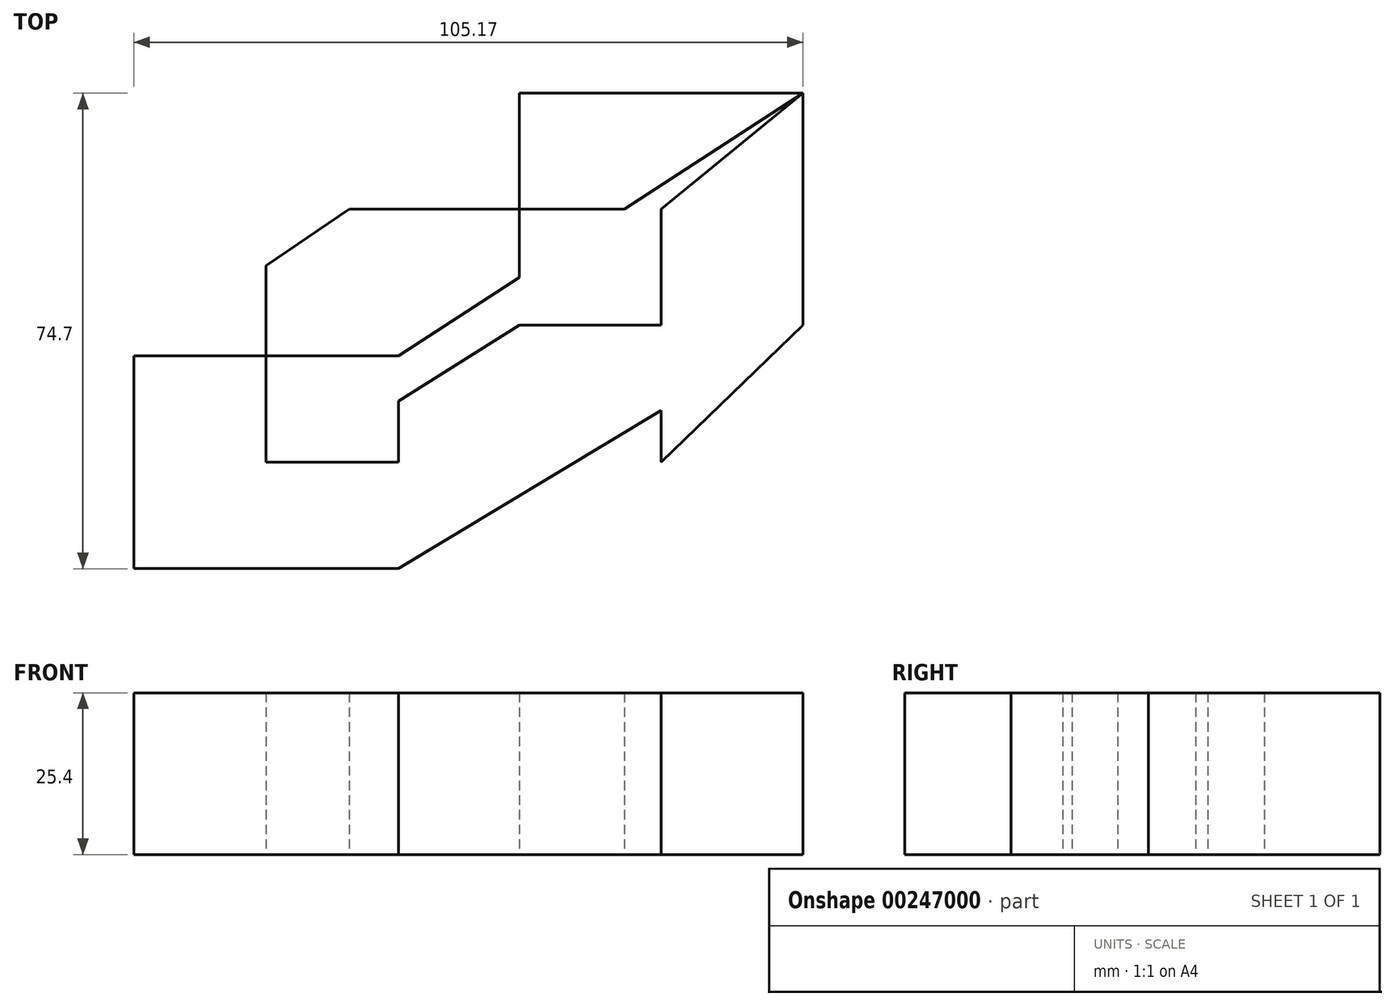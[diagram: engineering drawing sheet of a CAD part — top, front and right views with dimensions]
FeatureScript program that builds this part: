
annotation { "Feature Type Name" : "Feature", "Feature Type Description" : "" }
export const myFeature = defineFeature(function(context is Context, id is Id, definition is map)
    precondition{}
    {
        {
            var Q0;
            Q0=qCreatedBy(makeId("Top.planeOp"),FACE);
            var sketch = newSketch(context, id + "F0", { "sketchPlane" : qUnion([Q0])});
            skLineSegment(sketch, "E0.bottom", {"start": v(-31.03, 19.88) * mm, "end": v(31.03, 19.88) * mm});
            skLineSegment(sketch, "E0.top", {"start": v(-31.03, -19.88) * mm, "end": v(31.03, -19.88) * mm});
            skLineSegment(sketch, "E0.left", {"start": v(-31.03, 19.88) * mm, "end": v(-31.03, -19.88) * mm});
            skLineSegment(sketch, "E0.right", {"start": v(31.03, 19.88) * mm, "end": v(31.03, -19.88) * mm});
            skPoint(sketch, "E0.middle", {"position": v(0, 0) * mm});
            skLineSegment(sketch, "E1.bottom", {"start": v(8.73, 38.1) * mm, "end": v(53.33, 38.1) * mm});
            skLineSegment(sketch, "E1.top", {"start": v(8.73, 1.67) * mm, "end": v(53.33, 1.67) * mm});
            skLineSegment(sketch, "E1.left", {"start": v(8.73, 38.1) * mm, "end": v(8.73, 1.67) * mm});
            skLineSegment(sketch, "E1.right", {"start": v(53.33, 38.1) * mm, "end": v(53.33, 1.67) * mm});
            skPoint(sketch, "E1.middle", {"position": v(31.03, 19.88) * mm});
            skLineSegment(sketch, "E2", {"start": v(-31.03, 19.88) * mm, "end": v(8.73, 38.1) * mm});
            skLineSegment(sketch, "E3", {"start": v(31.03, 19.88) * mm, "end": v(53.33, 38.1) * mm});
            skLineSegment(sketch, "E4", {"start": v(8.73, 1.67) * mm, "end": v(-31.03, -19.88) * mm});
            skLineSegment(sketch, "E5", {"start": v(53.33, 1.67) * mm, "end": v(31.03, -19.88) * mm});
            skLineSegment(sketch, "E6.bottom", {"start": v(-51.84, -3.16) * mm, "end": v(-10.22, -3.16) * mm});
            skLineSegment(sketch, "E6.top", {"start": v(-51.84, -36.6) * mm, "end": v(-10.22, -36.6) * mm});
            skLineSegment(sketch, "E6.left", {"start": v(-51.84, -3.16) * mm, "end": v(-51.84, -36.6) * mm});
            skLineSegment(sketch, "E6.right", {"start": v(-10.22, -3.16) * mm, "end": v(-10.22, -36.6) * mm});
            skPoint(sketch, "E6.middle", {"position": v(-31.03, -19.88) * mm});
            skLineSegment(sketch, "E7", {"start": v(-51.84, -3.16) * mm, "end": v(8.73, 38.1) * mm});
            skLineSegment(sketch, "E8", {"start": v(-10.22, -3.16) * mm, "end": v(53.33, 38.1) * mm});
            skLineSegment(sketch, "E9", {"start": v(-51.84, -36.6) * mm, "end": v(8.73, 1.67) * mm});
            skLineSegment(sketch, "E10", {"start": v(-10.22, -36.6) * mm, "end": v(53.33, 1.67) * mm});
            skSolve(sketch);
        }
        {
            var Q0;
            {var subQ5=sQuery(id+"F0.wireOp",EDGE,"E7");var subQ8=sQuery(id+"F0.wireOp",EDGE,"E0.bottom");var subQ11=makeQuery(id+"F0.imprint","INTERSECT",VERTEX,{"derivedFrom":[subQ8,subQ5]});Q0=makeQuery(id+"F0.imprint","IMPRINT",FACE,{"disambiguationData":[TD([[makeQuery(id+"F0.imprint","IMPRINT",EDGE,{"disambiguationData":[TD([[subQ11,-1.0]])],"derivedFrom":subQ8}),-1.0]])]});}
            var Q1;
            {var subQ1=sQuery(id+"F0.wireOp",EDGE,"E0.top");var subQ9=sQuery(id+"F0.wireOp",EDGE,"E10");var subQ11=makeQuery(id+"F0.imprint","INTERSECT",VERTEX,{"derivedFrom":[subQ1,subQ9]});Q1=makeQuery(id+"F0.imprint","IMPRINT",FACE,{"disambiguationData":[TD([[makeQuery(id+"F0.imprint","IMPRINT",EDGE,{"disambiguationData":[TD([[subQ11,1.0]])],"derivedFrom":subQ1}),1.0]])]});}
            var Q2;
            {var subQ5=sQuery(id+"F0.wireOp",EDGE,"E1.bottom");Q2=makeQuery(id+"F0.imprint","IMPRINT",FACE,{"disambiguationData":[TD([[makeQuery(id+"F0.imprint","IMPRINT",EDGE,{"derivedFrom":subQ5}),-1.0]])]});}
            var Q3;
            {var subQ4=sQuery(id+"F0.wireOp",EDGE,"E1.right");Q3=makeQuery(id+"F0.imprint","IMPRINT",FACE,{"disambiguationData":[TD([[makeQuery(id+"F0.imprint","IMPRINT",EDGE,{"derivedFrom":subQ4}),-1.0]])]});}
            var Q4;
            {var subQ0=sQuery(id+"F0.wireOp",EDGE,"E1.top");var subQ1=sQuery(id+"F0.wireOp",EDGE,"E0.right");var subQ2=makeQuery(id+"F0.imprint","INTERSECT",VERTEX,{"derivedFrom":[subQ1,subQ0]});Q4=makeQuery(id+"F0.imprint","IMPRINT",FACE,{"disambiguationData":[TD([[makeQuery(id+"F0.imprint","IMPRINT",EDGE,{"disambiguationData":[TD([[subQ2,-1.0]])],"derivedFrom":subQ1}),1.0]])]});}
            var Q5;
            {var subQ0=sQuery(id+"F0.wireOp",EDGE,"E5");Q5=makeQuery(id+"F0.imprint","IMPRINT",FACE,{"disambiguationData":[TD([[makeQuery(id+"F0.imprint","IMPRINT",EDGE,{"derivedFrom":subQ0}),-1.0]])]});}
            var Q6;
            {var subQ5=sQuery(id+"F0.wireOp",EDGE,"E6.top");Q6=makeQuery(id+"F0.imprint","IMPRINT",FACE,{"disambiguationData":[TD([[makeQuery(id+"F0.imprint","IMPRINT",EDGE,{"derivedFrom":subQ5}),1.0]])]});}
            var Q7;
            {var subQ0=sQuery(id+"F0.wireOp",EDGE,"E10");var subQ1=sQuery(id+"F0.wireOp",EDGE,"E0.top");var subQ2=makeQuery(id+"F0.imprint","INTERSECT",VERTEX,{"derivedFrom":[subQ1,subQ0]});Q7=makeQuery(id+"F0.imprint","IMPRINT",FACE,{"disambiguationData":[TD([[makeQuery(id+"F0.imprint","IMPRINT",EDGE,{"disambiguationData":[TD([[subQ2,1.0]])],"derivedFrom":subQ1}),-1.0]])]});}
            var Q8;
            {var subQ0=sQuery(id+"F0.wireOp",EDGE,"E6.left");Q8=makeQuery(id+"F0.imprint","IMPRINT",FACE,{"disambiguationData":[TD([[makeQuery(id+"F0.imprint","IMPRINT",EDGE,{"derivedFrom":subQ0}),1.0]])]});}
            extrude(context, id + "F1", {"entities" : qUnion([Q0, Q1, Q2, Q3, Q4, Q5, Q6, Q7, Q8]), "depth" : 25.4 * mm});
        }
    });
